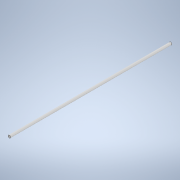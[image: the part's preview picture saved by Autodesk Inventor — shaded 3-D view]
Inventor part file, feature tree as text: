
AUTODESK INVENTOR PART (.ipt)
format: ipt  version: 2022 (Build 260153000, 153)  size: 91,648 bytes
history: native  units: in
note: dims shown in document units (in); Inventor stores cm internally (conversion verified against a paired STEP export)
features: extrude x1, sketch x1
ambient origin geometry x8: Origin, YZ Plane, XZ Plane, XY Plane, X Axis, Y Axis, Z Axis, Center Point
bodies: Solid1 (feature_tree)
feature tree (2):
  extrude  "Extrusion1"  Depth=6.5in TaperAngle=0.0deg
  sketch  "Sketch1"  dims[d0=0.1in d1=6.5in d2=0.0in]
